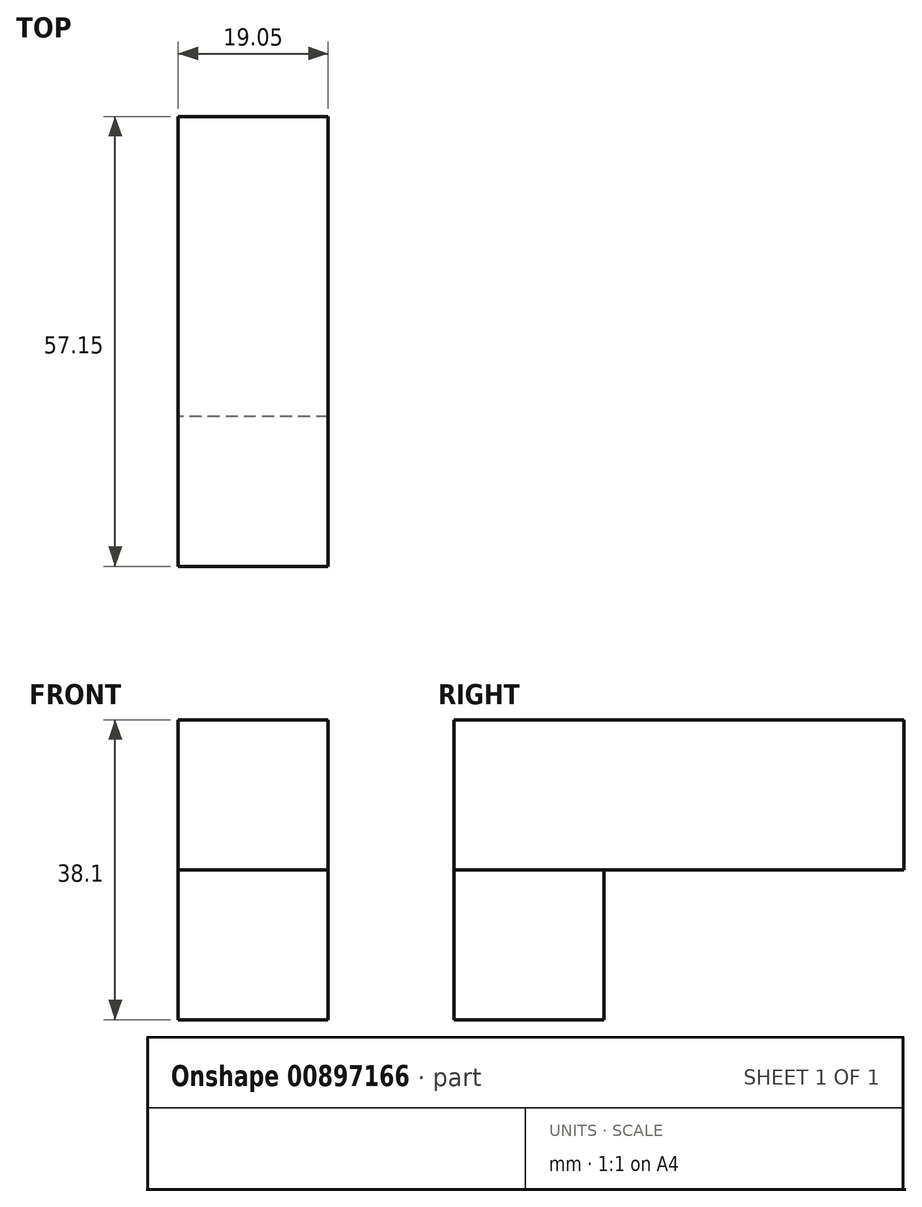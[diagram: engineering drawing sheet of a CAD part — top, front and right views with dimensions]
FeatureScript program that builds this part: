
annotation { "Feature Type Name" : "Feature", "Feature Type Description" : "" }
export const myFeature = defineFeature(function(context is Context, id is Id, definition is map)
    precondition{}
    {
        {
            var Q0;
            Q0=qCreatedBy(makeId("Front.planeOp"),FACE);
            var sketch = newSketch(context, id + "F0", { "sketchPlane" : qUnion([Q0])});
            skLineSegment(sketch, "E0", {"start": v(-53.16, 60.96) * mm, "end": v(-53.16, 41.91) * mm});
            skLineSegment(sketch, "E1", {"start": v(-53.16, 60.96) * mm, "end": v(-34.1, 60.96) * mm});
            skLineSegment(sketch, "E2", {"start": v(-34.1, 60.96) * mm, "end": v(-34.1, 41.91) * mm});
            skLineSegment(sketch, "E3", {"start": v(-34.1, 41.91) * mm, "end": v(-53.16, 41.91) * mm});
            skSolve(sketch);
        }
        {
            var Q0;
            Q0 = qSketchRegion(id + "F0", true);
            extrude(context, id + "F1", {"entities" : qUnion([Q0]), "depth" : 57.15 * mm, "offsetDistance" : 25.4 * mm});
        }
        {
            var Q0;
            Q0=qCreatedBy(makeId("Top.planeOp"),FACE);
            var sketch = newSketch(context, id + "F2", { "sketchPlane" : qUnion([Q0])});
            skLineSegment(sketch, "E4", {"start": v(-53.16, -57.15) * mm, "end": v(-53.16, -38.1) * mm});
            skLineSegment(sketch, "E5", {"start": v(-53.16, -57.15) * mm, "end": v(-34.1, -57.15) * mm});
            skLineSegment(sketch, "E6", {"start": v(-34.1, -57.15) * mm, "end": v(-34.1, -38.1) * mm});
            skLineSegment(sketch, "E7", {"start": v(-34.1, -38.1) * mm, "end": v(-53.16, -38.1) * mm});
            skSolve(sketch);
        }
        {
            var Q0;
            Q0 = qSketchRegion(id + "F2", true);
            extrude(context, id + "F3", {"entities" : qUnion([Q0]), "depth" : 19.05 * mm, "offsetDistance" : 25.4 * mm});
        }
        {
            var Q0;
            Q0=makeQuery(id+"F3.opExtrude","SWEPT_BODY",BODY,{"disambiguationData":[OSD([sQuery(id+"F2.wireOp",EDGE,"E4"),sQuery(id+"F2.wireOp",EDGE,"E5"),sQuery(id+"F2.wireOp",EDGE,"E6"),sQuery(id+"F2.wireOp",EDGE,"E7")])]});
            transform(context, id + "F4", {"entities" : qUnion([Q0]), "transformType" : TransformType.TRANSLATION_3D, "dx" : 0 * mm, "dy" : 0 * mm, "dz" : 22.86 * mm, "makeCopy" : false});
        }
    });
